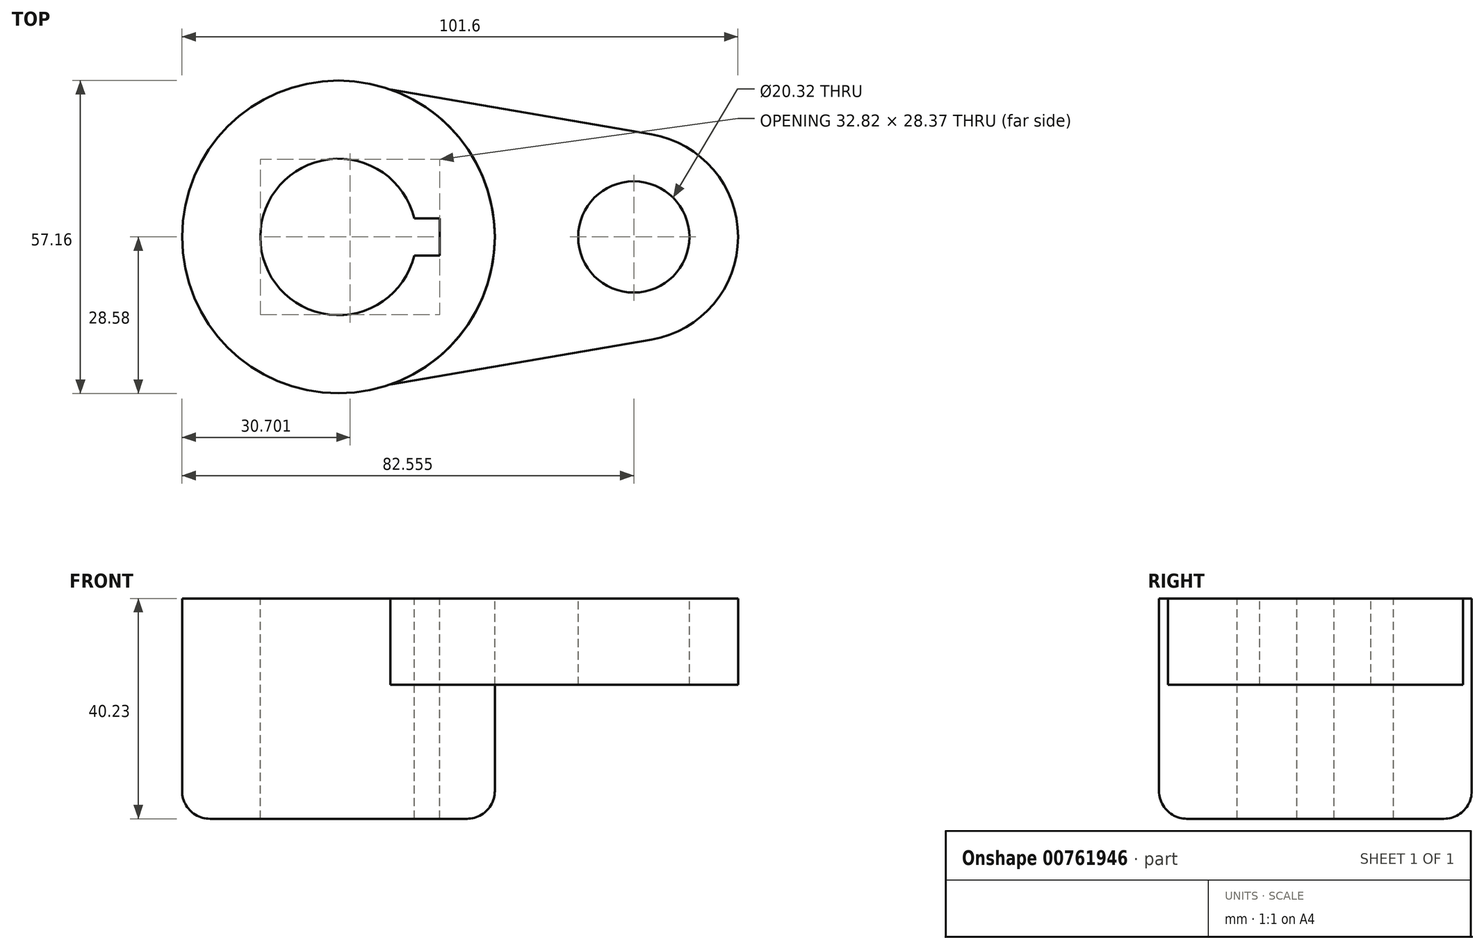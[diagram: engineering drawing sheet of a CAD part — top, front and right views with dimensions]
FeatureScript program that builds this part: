
annotation { "Feature Type Name" : "Feature", "Feature Type Description" : "" }
export const myFeature = defineFeature(function(context is Context, id is Id, definition is map)
    precondition{}
    {
        {
            var Q0;
            Q0=qCreatedBy(makeId("Top.planeOp"),FACE);
            var sketch = newSketch(context, id + "F0", { "sketchPlane" : qUnion([Q0])});
            skArc(sketch, "E0", {"start": v(-21.94, 3.4) * mm, "mid": v(-50.1, 0) * mm, "end": v(-21.94, -3.4) * mm});
            skCircle(sketch, "E1", {"center": v(-35.82, 0) * mm, "radius": 28.58 * mm});
            skCircle(sketch, "E2", {"center": v(-35.82, 0) * mm, "radius": 25.44 * mm});
            skLineSegment(sketch, "E3.bottom", {"start": v(-17.3, -3.4) * mm, "end": v(-21.94, -3.4) * mm});
            skLineSegment(sketch, "E3.top", {"start": v(-17.3, 3.4) * mm, "end": v(-21.94, 3.4) * mm});
            skLineSegment(sketch, "E3.left", {"start": v(-17.3, -3.4) * mm, "end": v(-17.3, 3.4) * mm});
            skPoint(sketch, "E3.right.end.orphan", {"position": v(-54.35, 3.4) * mm});
            skPoint(sketch, "E4.trimOffspring.end.orphan", {"position": v(-54.35, -3.4) * mm});
            skPoint(sketch, "E5.orphan", {"position": v(-50.1, 0) * mm});
            skPoint(sketch, "E6.end.orphan", {"position": v(-17.3, 0) * mm});
            skCircle(sketch, "E7", {"center": v(18.15, 0) * mm, "radius": 10.16 * mm});
            skArc(sketch, "E8", {"start": v(21.37, -18.78) * mm, "mid": v(37.2, 0) * mm, "end": v(21.37, 18.78) * mm});
            skLineSegment(sketch, "E9", {"start": v(-26.3, -26.95) * mm, "end": v(21.37, -18.78) * mm});
            skLineSegment(sketch, "E10", {"start": v(-26.3, 26.95) * mm, "end": v(21.37, 18.78) * mm});
            skPoint(sketch, "E11.orphan", {"position": v(-35.82, -28.58) * mm});
            skPoint(sketch, "E12.orphan", {"position": v(-35.82, 28.58) * mm});
            skSolve(sketch);
        }
        {
            var Q0;
            Q0=makeQuery(id+"F0.imprint","IMPRINT",FACE,{"disambiguationData":[TD([[makeQuery(id+"F0.imprint","IMPRINT",EDGE,{"derivedFrom":sQuery(id+"F0.wireOp",EDGE,"E0")}),-1.0]])]});
            var Q1;
            Q1=makeQuery(id+"F0.imprint","IMPRINT",FACE,{"disambiguationData":[TD([[makeQuery(id+"F0.imprint","IMPRINT",EDGE,{"derivedFrom":sQuery(id+"F0.wireOp",EDGE,"E2")}),-1.0]])]});
            extrude(context, id + "F1", {"entities" : qUnion([Q0, Q1]), "oppositeDirection" : true, "depth" : 40.23 * mm, "offsetDistance" : 25.4 * mm});
        }
        {
            var Q0;
            Q0=makeQuery(id+"F0.imprint","IMPRINT",FACE,{"disambiguationData":[TD([[makeQuery(id+"F0.imprint","IMPRINT",EDGE,{"derivedFrom":sQuery(id+"F0.wireOp",EDGE,"E7")}),-1.0]])]});
            extrude(context, id + "F2", {"entities" : qUnion([Q0]), "oppositeDirection" : true, "depth" : 15.77 * mm, "offsetDistance" : 25.4 * mm});
        }
        {
            var Q0;
            Q0=makeQuery(id+"F1.opExtrude","CAP_EDGE",EDGE,{"disambiguationData":[OSD([sQuery(id+"F0.wireOp",EDGE,"E1")])],"isStart":false});
            fillet(context, id + "F3", {"entities" : qUnion([Q0]), "radius" : 5.08 * mm, "tangentPropagation" : true, "allowEdgeOverflow" : false});
        }
    });
